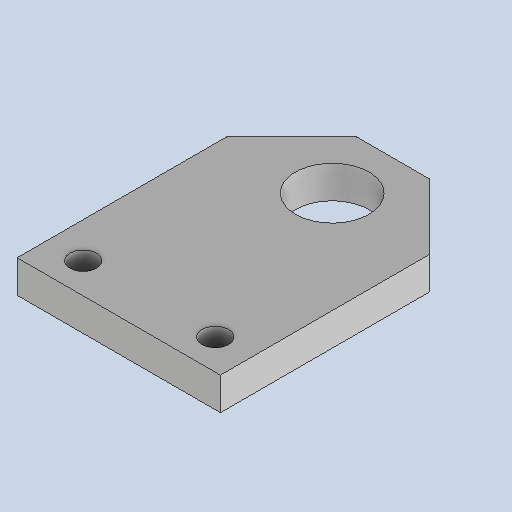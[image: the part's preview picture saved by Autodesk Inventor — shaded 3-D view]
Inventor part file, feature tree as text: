
AUTODESK INVENTOR PART (.ipt)
format: ipt  version: 2025 (Build 290162010, 162A)  size: 111,616 bytes
history: native  units: mm
features: sheet_metal_op x1, sketch x1, other x1
ambient origin geometry x8: Origin, YZ Plane, XZ Plane, XY Plane, X Axis, Y Axis, Z Axis, Center Point
bodies: Solid1 (feature_tree)
feature tree (3):
  sheet_metal_op  "Face1"
  sketch  "Sketch1"  dims[d0=100.0mm d1=36.1mm d2=105.0mm d3=32.0mm d4=135.0mm d6=45.0deg d7=13.0mm d8=65.0mm d9=15.0mm d10=16.0mm]
  other  "Plate1"
